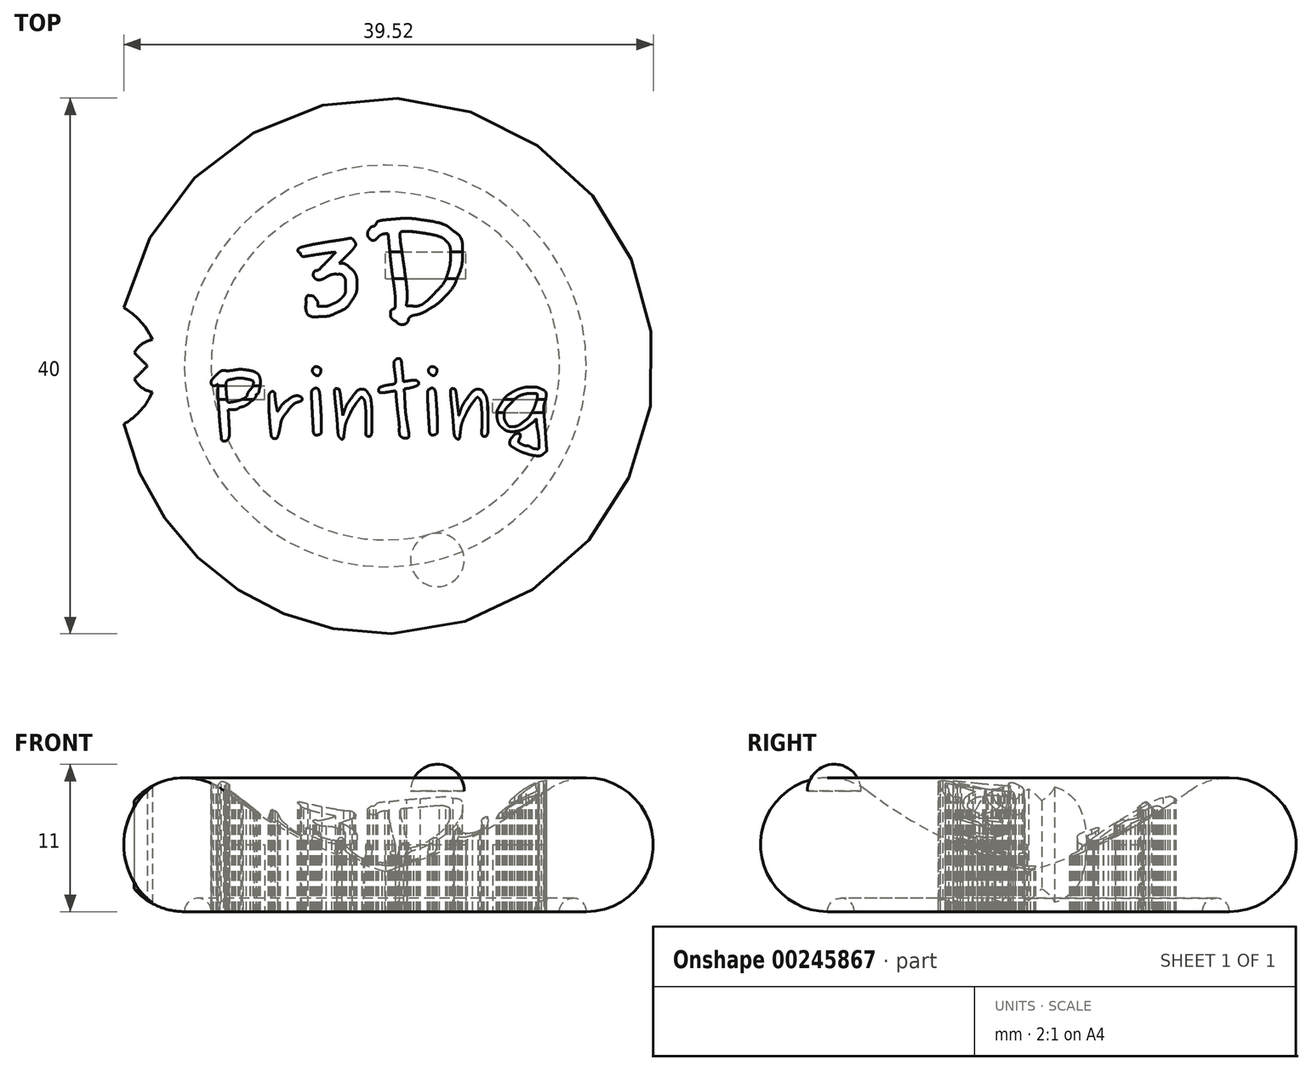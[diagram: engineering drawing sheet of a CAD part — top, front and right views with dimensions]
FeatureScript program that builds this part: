
annotation { "Feature Type Name" : "Feature", "Feature Type Description" : "" }
export const myFeature = defineFeature(function(context is Context, id is Id, definition is map)
    precondition{}
    {
        {
            var Q0;
            Q0=qCreatedBy(makeId("Front.planeOp"),FACE);
            var sketch = newSketch(context, id + "F0", { "sketchPlane" : qUnion([Q0])});
            skArc(sketch, "E0", {"start": v(-12, 9) * mm, "mid": v(-19.74, 6.58) * mm, "end": v(-15, 0) * mm});
            skLineSegment(sketch, "E1", {"start": v(-15, 0) * mm, "end": v(0, 0) * mm});
            skLineSegment(sketch, "E2", {"start": v(0, 0) * mm, "end": v(0, 3) * mm});
            skArc(sketch, "E3", {"start": v(-12, 9) * mm, "mid": v(-6.27, 5.46) * mm, "end": v(0, 3) * mm});
            skArc(sketch, "E4", {"start": v(-13, 0) * mm, "mid": v(-14, 1) * mm, "end": v(-15, 0) * mm});
            skSolve(sketch);
        }
        {
            var Q0;
            {var subQ3=sQuery(id+"F0.wireOp",EDGE,"E0");Q0=makeQuery(id+"F0.imprint","IMPRINT",FACE,{"disambiguationData":[TD([[makeQuery(id+"F0.imprint","IMPRINT",EDGE,{"derivedFrom":subQ3}),1.0]])]});}
            var Q1;
            Q1=sQuery(id+"F0.wireOp",EDGE,"E2");
            revolve(context, id + "F1", {"entities" : qUnion([Q0]), "axis" : qUnion([Q1]), "revolveType" : RevolveType.FULL});
        }
        {
            var Q0;
            Q0=qCreatedBy(makeId("Top.planeOp"),FACE);
            var sketch = newSketch(context, id + "F2", { "sketchPlane" : qUnion([Q0])});
            skCircle(sketch, "E5", {"center": v(-22, 0) * mm, "radius": 5 * mm});
            skCircle(sketch, "E6", {"center": v(-17, 0) * mm, "radius": 2 * mm});
            skLineSegment(sketch, "E7.bottom", {"start": v(-26.24, 0) * mm, "end": v(-22, 4.24) * mm});
            skLineSegment(sketch, "E7.top", {"start": v(-22, -4.24) * mm, "end": v(-17.76, 0) * mm});
            skLineSegment(sketch, "E7.left", {"start": v(-26.24, 0) * mm, "end": v(-22, -4.24) * mm});
            skLineSegment(sketch, "E7.right", {"start": v(-22, 4.24) * mm, "end": v(-17.76, 0) * mm});
            skLineSegment(sketch, "E8", {"start": v(-26.24, 0) * mm, "end": v(-17.76, 0) * mm, "construction": true});
            skSolve(sketch);
        }
        {
            var Q0;
            {var subQ0=sQuery(id+"F2.wireOp",EDGE,"E7.right");var subQ1=sQuery(id+"F2.wireOp",EDGE,"E6");var subQ2=makeQuery(id+"F2.imprint","INTERSECT",VERTEX,{"derivedFrom":[subQ1,subQ0]});Q0=makeQuery(id+"F2.imprint","IMPRINT",FACE,{"disambiguationData":[TD([[makeQuery(id+"F2.imprint","IMPRINT",EDGE,{"disambiguationData":[TD([[subQ2,-1.0]])],"derivedFrom":subQ1}),1.0]])]});}
            var Q1;
            {var subQ4=sQuery(id+"F2.wireOp",EDGE,"E7.bottom");Q1=makeQuery(id+"F2.imprint","IMPRINT",FACE,{"disambiguationData":[TD([[makeQuery(id+"F2.imprint","IMPRINT",EDGE,{"derivedFrom":subQ4}),-1.0]])]});}
            var Q2;
            {var subQ0=sQuery(id+"F2.wireOp",EDGE,"E7.bottom");Q2=makeQuery(id+"F2.imprint","IMPRINT",FACE,{"disambiguationData":[TD([[makeQuery(id+"F2.imprint","IMPRINT",EDGE,{"derivedFrom":subQ0}),1.0]])]});}
            extrude(context, id + "F3", {"entities" : qUnion([Q0, Q1, Q2]), "operationType" : NewBodyOperationType.REMOVE, "depth" : 25 * mm});
        }
        {
            var Q0;
            Q0=qCreatedBy(makeId("Right.planeOp"),FACE);
            var sketch = newSketch(context, id + "F4", { "sketchPlane" : qUnion([Q0])});
            skArc(sketch, "E9", {"start": v(-15, 11) * mm, "mid": v(-16.41, 10.41) * mm, "end": v(-17, 9) * mm});
            skLineSegment(sketch, "E10", {"start": v(-15, 11) * mm, "end": v(-15, 9) * mm});
            skLineSegment(sketch, "E11", {"start": v(-15, 9) * mm, "end": v(-17, 9) * mm});
            skSolve(sketch);
        }
        {
            var Q0;
            Q0=makeQuery(id+"F4.imprint","IMPRINT",FACE,{"disambiguationData":[TD([[makeQuery(id+"F4.imprint","IMPRINT",EDGE,{"derivedFrom":sQuery(id+"F4.wireOp",EDGE,"E9")}),1.0]])]});
            var Q1;
            Q1=sQuery(id+"F4.wireOp",EDGE,"E9");
            var Q2;
            Q2=sQuery(id+"F4.wireOp",EDGE,"E10");
            revolve(context, id + "F5", {"entities" : qUnion([Q0]), "surfaceEntities" : qUnion([Q1]), "axis" : qUnion([Q2]), "revolveType" : RevolveType.FULL});
        }
        {
            var Q0;
            Q0=qCreatedBy(makeId("Top.planeOp"),FACE);
            cPlane(context, id + "F6", {"entities" : qUnion([Q0]), "cplaneType" : CPlaneType.OFFSET, "offset" : 25 * mm, "width" : 150 * mm, "height" : 150 * mm});
        }
        {
            var Q0;
            Q0=qCreatedBy(id+"F6.planeOp",FACE);
            var sketch = newSketch(context, id + "F7", { "sketchPlane" : qUnion([Q0])});
            skFitSpline(sketch, "E12", {"points": [v(-4.86, 3.7) * mm, v(-5.56, 3.7) * mm, v(-5.9, 4.05) * mm, v(-5.9, 4.76) * mm]});
            skFitSpline(sketch, "E13", {"points": [v(-5.9, 4.76) * mm, v(-5.9, 5.08) * mm, v(-5.81, 5.24) * mm, v(-5.62, 5.24) * mm]});
            skFitSpline(sketch, "E14", {"points": [v(-5.62, 5.24) * mm, v(-5.46, 5.24) * mm, v(-5.33, 5.17) * mm, v(-5.21, 5.02) * mm]});
            skFitSpline(sketch, "E15", {"points": [v(-5.21, 5.02) * mm, v(-5.1, 4.86) * mm, v(-5.03, 4.7) * mm, v(-5.03, 4.55) * mm]});
            skFitSpline(sketch, "E16", {"points": [v(-5.03, 4.55) * mm, v(-5.03, 4.5) * mm, v(-5.02, 4.46) * mm, v(-5, 4.45) * mm]});
            skFitSpline(sketch, "E17", {"points": [v(-5, 4.45) * mm, v(-4.98, 4.44) * mm, v(-4.91, 4.44) * mm, v(-4.8, 4.44) * mm]});
            skFitSpline(sketch, "E18", {"points": [v(-4.8, 4.44) * mm, v(-4.51, 4.44) * mm, v(-4.24, 4.5) * mm, v(-3.98, 4.6) * mm]});
            skFitSpline(sketch, "E19", {"points": [v(-3.98, 4.6) * mm, v(-3.72, 4.72) * mm, v(-3.54, 4.82) * mm, v(-3.44, 4.9) * mm]});
            skFitSpline(sketch, "E20", {"points": [v(-3.44, 4.9) * mm, v(-3.34, 5) * mm, v(-3.26, 5.07) * mm, v(-3.2, 5.14) * mm]});
            skFitSpline(sketch, "E21", {"points": [v(-3.2, 5.14) * mm, v(-3.05, 5.31) * mm, v(-2.98, 5.6) * mm, v(-2.98, 5.98) * mm]});
            skFitSpline(sketch, "E22", {"points": [v(-2.98, 5.98) * mm, v(-2.98, 6.34) * mm, v(-3.02, 6.57) * mm, v(-3.12, 6.68) * mm]});
            skFitSpline(sketch, "E23", {"points": [v(-3.12, 6.68) * mm, v(-3.21, 6.79) * mm, v(-3.36, 6.84) * mm, v(-3.56, 6.84) * mm]});
            skFitSpline(sketch, "E24", {"points": [v(-3.56, 6.84) * mm, v(-3.87, 6.84) * mm, v(-4.15, 6.77) * mm, v(-4.4, 6.63) * mm]});
            skFitSpline(sketch, "E25", {"points": [v(-4.4, 6.63) * mm, v(-4.64, 6.5) * mm, v(-4.81, 6.43) * mm, v(-4.92, 6.43) * mm]});
            skFitSpline(sketch, "E26", {"points": [v(-4.92, 6.43) * mm, v(-5.07, 6.43) * mm, v(-5.18, 6.47) * mm, v(-5.26, 6.55) * mm]});
            skFitSpline(sketch, "E27", {"points": [v(-5.26, 6.55) * mm, v(-5.34, 6.63) * mm, v(-5.38, 6.72) * mm, v(-5.38, 6.83) * mm]});
            skFitSpline(sketch, "E28", {"points": [v(-5.38, 6.83) * mm, v(-5.38, 6.91) * mm, v(-5.36, 6.98) * mm, v(-5.31, 7.04) * mm]});
            skFitSpline(sketch, "E29", {"points": [v(-5.31, 7.04) * mm, v(-5.27, 7.1) * mm, v(-5.21, 7.12) * mm, v(-5.14, 7.12) * mm]});
            skFitSpline(sketch, "E30", {"points": [v(-5.14, 7.12) * mm, v(-5.04, 7.14) * mm, v(-4.8, 7.34) * mm, v(-4.43, 7.72) * mm]});
            skFitSpline(sketch, "E31", {"points": [v(-4.43, 7.72) * mm, v(-4.06, 8.1) * mm, v(-3.82, 8.36) * mm, v(-3.72, 8.5) * mm]});
            skFitSpline(sketch, "E32", {"points": [v(-3.72, 8.5) * mm, v(-3.94, 8.48) * mm, v(-4.25, 8.44) * mm, v(-4.63, 8.39) * mm]});
            skFitSpline(sketch, "E33", {"points": [v(-4.63, 8.39) * mm, v(-5, 8.33) * mm, v(-5.34, 8.28) * mm, v(-5.62, 8.23) * mm]});
            skFitSpline(sketch, "E34", {"points": [v(-5.62, 8.23) * mm, v(-5.91, 8.19) * mm, v(-6.07, 8.17) * mm, v(-6.1, 8.17) * mm]});
            skFitSpline(sketch, "E35", {"points": [v(-6.1, 8.17) * mm, v(-6.17, 8.17) * mm, v(-6.23, 8.19) * mm, v(-6.26, 8.22) * mm]});
            skFitSpline(sketch, "E36", {"points": [v(-6.26, 8.22) * mm, v(-6.3, 8.27) * mm, v(-6.32, 8.31) * mm, v(-6.33, 8.37) * mm]});
            skFitSpline(sketch, "E37", {"points": [v(-6.34, 8.44) * mm, v(-6.4, 8.45) * mm, v(-6.44, 8.47) * mm, v(-6.48, 8.5) * mm]});
            skFitSpline(sketch, "E38", {"points": [v(-6.48, 8.5) * mm, v(-6.52, 8.53) * mm, v(-6.54, 8.58) * mm, v(-6.54, 8.63) * mm]});
            skFitSpline(sketch, "E39", {"points": [v(-6.54, 8.63) * mm, v(-6.53, 8.7) * mm, v(-6.5, 8.75) * mm, v(-6.45, 8.78) * mm]});
            skFitSpline(sketch, "E40", {"points": [v(-6.45, 8.78) * mm, v(-6.36, 8.83) * mm, v(-6.15, 8.9) * mm, v(-5.8, 8.98) * mm]});
            skFitSpline(sketch, "E41", {"points": [v(-5.8, 8.98) * mm, v(-5.45, 9.06) * mm, v(-5.1, 9.13) * mm, v(-4.76, 9.18) * mm]});
            skFitSpline(sketch, "E42", {"points": [v(-4.76, 9.18) * mm, v(-4.4, 9.24) * mm, v(-4.05, 9.3) * mm, v(-3.69, 9.36) * mm]});
            skFitSpline(sketch, "E43", {"points": [v(-3.69, 9.36) * mm, v(-3.33, 9.41) * mm, v(-3.13, 9.44) * mm, v(-3.1, 9.45) * mm]});
            skFitSpline(sketch, "E44", {"points": [v(-3.1, 9.45) * mm, v(-2.8, 9.5) * mm, v(-2.65, 9.53) * mm, v(-2.64, 9.53) * mm]});
            skFitSpline(sketch, "E45", {"points": [v(-2.64, 9.53) * mm, v(-2.53, 9.53) * mm, v(-2.44, 9.47) * mm, v(-2.35, 9.36) * mm]});
            skFitSpline(sketch, "E46", {"points": [v(-2.35, 9.36) * mm, v(-2.26, 9.25) * mm, v(-2.22, 9.15) * mm, v(-2.22, 9.06) * mm]});
            skFitSpline(sketch, "E47", {"points": [v(-2.22, 9.06) * mm, v(-2.22, 9.02) * mm, v(-2.24, 8.96) * mm, v(-2.3, 8.88) * mm]});
            skFitSpline(sketch, "E48", {"points": [v(-2.3, 8.88) * mm, v(-2.34, 8.8) * mm, v(-2.41, 8.72) * mm, v(-2.5, 8.6) * mm]});
            skFitSpline(sketch, "E49", {"points": [v(-2.5, 8.6) * mm, v(-2.6, 8.5) * mm, v(-2.7, 8.4) * mm, v(-2.8, 8.31) * mm]});
            skFitSpline(sketch, "E50", {"points": [v(-2.8, 8.31) * mm, v(-2.88, 8.23) * mm, v(-3, 8.12) * mm, v(-3.13, 7.98) * mm]});
            skFitSpline(sketch, "E51", {"points": [v(-3.13, 7.98) * mm, v(-3.27, 7.84) * mm, v(-3.38, 7.73) * mm, v(-3.45, 7.65) * mm]});
            skLineSegment(sketch, "E52", {"start": v(-6.33, 8.37) * mm, "end": v(-6.34, 8.44) * mm});
            skLineSegment(sketch, "E53", {"start": v(-6.34, 8.44) * mm, "end": v(-6.33, 8.37) * mm});
            skFitSpline(sketch, "E54", {"points": [v(-3.32, 7.65) * mm, v(-3.1, 7.65) * mm, v(-2.88, 7.53) * mm, v(-2.63, 7.3) * mm]});
            skFitSpline(sketch, "E55", {"points": [v(-2.63, 7.3) * mm, v(-2.38, 7.1) * mm, v(-2.22, 6.86) * mm, v(-2.15, 6.62) * mm]});
            skFitSpline(sketch, "E56", {"points": [v(-2.15, 6.62) * mm, v(-2.13, 6.53) * mm, v(-2.12, 6.4) * mm, v(-2.12, 6.26) * mm]});
            skFitSpline(sketch, "E57", {"points": [v(-2.12, 6.26) * mm, v(-2.12, 5.74) * mm, v(-2.25, 5.26) * mm, v(-2.53, 4.84) * mm]});
            skFitSpline(sketch, "E58", {"points": [v(-2.53, 4.84) * mm, v(-2.75, 4.5) * mm, v(-3.09, 4.22) * mm, v(-3.54, 4.01) * mm]});
            skFitSpline(sketch, "E59", {"points": [v(-3.54, 4.01) * mm, v(-4, 3.8) * mm, v(-4.44, 3.7) * mm, v(-4.86, 3.7) * mm]});
            skLineSegment(sketch, "E60", {"start": v(-3.45, 7.65) * mm, "end": v(-3.32, 7.65) * mm});
            skLineSegment(sketch, "E61", {"start": v(-3.32, 7.65) * mm, "end": v(-3.45, 7.65) * mm});
            skFitSpline(sketch, "E62", {"points": [v(1.44, 10.04) * mm, v(1.3, 10.04) * mm, v(1.2, 10.03) * mm, v(1.16, 10) * mm]});
            skFitSpline(sketch, "E63", {"points": [v(1.16, 10) * mm, v(1.12, 9.96) * mm, v(1.1, 9.89) * mm, v(1.1, 9.76) * mm]});
            skFitSpline(sketch, "E64", {"points": [v(1.1, 9.76) * mm, v(1.1, 9.56) * mm, v(1.2, 8.85) * mm, v(1.36, 7.61) * mm]});
            skFitSpline(sketch, "E65", {"points": [v(1.36, 7.61) * mm, v(1.54, 6.38) * mm, v(1.63, 5.57) * mm, v(1.63, 5.2) * mm]});
            skFitSpline(sketch, "E66", {"points": [v(1.63, 5.2) * mm, v(1.63, 5.06) * mm, v(1.62, 4.93) * mm, v(1.6, 4.8) * mm]});
            skFitSpline(sketch, "E67", {"points": [v(1.93, 4.48) * mm, v(2.47, 4.48) * mm, v(3.1, 4.85) * mm, v(3.82, 5.6) * mm]});
            skFitSpline(sketch, "E68", {"points": [v(3.82, 5.6) * mm, v(4.23, 6.01) * mm, v(4.5, 6.44) * mm, v(4.64, 6.87) * mm]});
            skFitSpline(sketch, "E69", {"points": [v(4.64, 6.87) * mm, v(4.78, 7.3) * mm, v(4.85, 7.83) * mm, v(4.85, 8.46) * mm]});
            skFitSpline(sketch, "E70", {"points": [v(4.85, 8.46) * mm, v(4.85, 8.71) * mm, v(4.83, 8.88) * mm, v(4.8, 8.97) * mm]});
            skFitSpline(sketch, "E71", {"points": [v(4.8, 8.97) * mm, v(4.76, 9.06) * mm, v(4.67, 9.18) * mm, v(4.53, 9.33) * mm]});
            skFitSpline(sketch, "E72", {"points": [v(4.53, 9.33) * mm, v(4.39, 9.47) * mm, v(4.22, 9.58) * mm, v(4.05, 9.65) * mm]});
            skFitSpline(sketch, "E73", {"points": [v(4.05, 9.65) * mm, v(3.88, 9.71) * mm, v(3.59, 9.78) * mm, v(3.18, 9.86) * mm]});
            skFitSpline(sketch, "E74", {"points": [v(3.18, 9.86) * mm, v(2.4, 9.98) * mm, v(1.83, 10.04) * mm, v(1.44, 10.04) * mm]});
            skLineSegment(sketch, "E75", {"start": v(1.6, 4.8) * mm, "end": v(1.55, 4.48) * mm});
            skLineSegment(sketch, "E76", {"start": v(1.55, 4.48) * mm, "end": v(1.93, 4.48) * mm});
            skFitSpline(sketch, "E77", {"points": [v(-1.33, 9.83) * mm, v(-1.32, 9.98) * mm, v(-1.27, 10.11) * mm, v(-1.17, 10.23) * mm]});
            skFitSpline(sketch, "E78", {"points": [v(-1.17, 10.23) * mm, v(-1.07, 10.36) * mm, v(-0.97, 10.42) * mm, v(-0.88, 10.42) * mm]});
            skFitSpline(sketch, "E79", {"points": [v(-0.88, 10.42) * mm, v(-0.82, 10.44) * mm, v(-0.76, 10.5) * mm, v(-0.7, 10.58) * mm]});
            skFitSpline(sketch, "E80", {"points": [v(-0.7, 10.58) * mm, v(-0.59, 10.76) * mm, v(-0.26, 10.87) * mm, v(0.28, 10.93) * mm]});
            skFitSpline(sketch, "E81", {"points": [v(0.28, 10.93) * mm, v(0.92, 10.99) * mm, v(1.36, 11.02) * mm, v(1.6, 11.02) * mm]});
            skFitSpline(sketch, "E82", {"points": [v(1.6, 11.02) * mm, v(1.88, 11.02) * mm, v(2.22, 10.98) * mm, v(2.62, 10.92) * mm]});
            skFitSpline(sketch, "E83", {"points": [v(2.62, 10.92) * mm, v(3.77, 10.74) * mm, v(4.58, 10.46) * mm, v(5.04, 10.1) * mm]});
            skFitSpline(sketch, "E84", {"points": [v(5.04, 10.1) * mm, v(5.51, 9.74) * mm, v(5.75, 9.2) * mm, v(5.75, 8.46) * mm]});
            skFitSpline(sketch, "E85", {"points": [v(5.75, 8.46) * mm, v(5.75, 7.83) * mm, v(5.63, 7.23) * mm, v(5.4, 6.66) * mm]});
            skFitSpline(sketch, "E86", {"points": [v(5.4, 6.66) * mm, v(5.17, 6.1) * mm, v(4.87, 5.62) * mm, v(4.5, 5.24) * mm]});
            skFitSpline(sketch, "E87", {"points": [v(4.5, 5.24) * mm, v(4.14, 4.85) * mm, v(3.75, 4.54) * mm, v(3.33, 4.29) * mm]});
            skFitSpline(sketch, "E88", {"points": [v(3.33, 4.29) * mm, v(2.93, 4.04) * mm, v(2.52, 3.87) * mm, v(2.13, 3.78) * mm]});
            skFitSpline(sketch, "E89", {"points": [v(2.13, 3.78) * mm, v(2, 3.75) * mm, v(1.9, 3.7) * mm, v(1.83, 3.64) * mm]});
            skFitSpline(sketch, "E90", {"points": [v(1.83, 3.64) * mm, v(1.76, 3.57) * mm, v(1.72, 3.5) * mm, v(1.72, 3.45) * mm]});
            skFitSpline(sketch, "E91", {"points": [v(1.72, 3.45) * mm, v(1.71, 3.38) * mm, v(1.69, 3.32) * mm, v(1.64, 3.26) * mm]});
            skFitSpline(sketch, "E92", {"points": [v(1.64, 3.26) * mm, v(1.6, 3.2) * mm, v(1.54, 3.15) * mm, v(1.44, 3.12) * mm]});
            skFitSpline(sketch, "E93", {"points": [v(1.44, 3.12) * mm, v(1.38, 3.1) * mm, v(1.32, 3.09) * mm, v(1.25, 3.09) * mm]});
            skFitSpline(sketch, "E94", {"points": [v(1.25, 3.09) * mm, v(1.14, 3.09) * mm, v(1.05, 3.11) * mm, v(0.97, 3.15) * mm]});
            skFitSpline(sketch, "E95", {"points": [v(0.97, 3.15) * mm, v(0.9, 3.19) * mm, v(0.86, 3.24) * mm, v(0.85, 3.3) * mm]});
            skFitSpline(sketch, "E96", {"points": [v(0.71, 3.36) * mm, v(0.62, 3.4) * mm, v(0.54, 3.47) * mm, v(0.48, 3.55) * mm]});
            skFitSpline(sketch, "E97", {"points": [v(0.48, 3.55) * mm, v(0.41, 3.62) * mm, v(0.38, 3.72) * mm, v(0.38, 3.85) * mm]});
            skFitSpline(sketch, "E98", {"points": [v(0.38, 3.85) * mm, v(0.38, 4.06) * mm, v(0.47, 4.2) * mm, v(0.63, 4.26) * mm]});
            skFitSpline(sketch, "E99", {"points": [v(0.63, 4.26) * mm, v(0.7, 4.3) * mm, v(0.73, 4.52) * mm, v(0.73, 4.9) * mm]});
            skFitSpline(sketch, "E100", {"points": [v(0.73, 4.9) * mm, v(0.73, 5.14) * mm, v(0.72, 5.39) * mm, v(0.69, 5.64) * mm]});
            skFitSpline(sketch, "E101", {"points": [v(0.69, 5.64) * mm, v(0.66, 5.89) * mm, v(0.6, 6.26) * mm, v(0.53, 6.77) * mm]});
            skFitSpline(sketch, "E102", {"points": [v(0.53, 6.77) * mm, v(0.46, 7.28) * mm, v(0.4, 7.85) * mm, v(0.34, 8.47) * mm]});
            skLineSegment(sketch, "E103", {"start": v(0.85, 3.3) * mm, "end": v(0.71, 3.36) * mm});
            skLineSegment(sketch, "E104", {"start": v(0.71, 3.36) * mm, "end": v(0.85, 3.3) * mm});
            skFitSpline(sketch, "E105", {"points": [v(0, 9.87) * mm, v(-0.2, 9.84) * mm, v(-0.38, 9.75) * mm, v(-0.55, 9.6) * mm]});
            skFitSpline(sketch, "E106", {"points": [v(-0.55, 9.6) * mm, v(-0.72, 9.44) * mm, v(-0.84, 9.36) * mm, v(-0.91, 9.36) * mm]});
            skFitSpline(sketch, "E107", {"points": [v(-0.91, 9.36) * mm, v(-1, 9.36) * mm, v(-1.08, 9.42) * mm, v(-1.19, 9.52) * mm]});
            skFitSpline(sketch, "E108", {"points": [v(-1.19, 9.52) * mm, v(-1.28, 9.63) * mm, v(-1.33, 9.73) * mm, v(-1.33, 9.83) * mm]});
            skLineSegment(sketch, "E109", {"start": v(0.34, 8.47) * mm, "end": v(0.2, 9.89) * mm});
            skLineSegment(sketch, "E110", {"start": v(0.2, 9.89) * mm, "end": v(0, 9.87) * mm});
            skFitSpline(sketch, "E111", {"points": [v(-9.86, -1.36) * mm, v(-9.86, -1.18) * mm, v(-10.03, -1.05) * mm, v(-10.39, -0.98) * mm]});
            skFitSpline(sketch, "E112", {"points": [v(-10.39, -0.98) * mm, v(-10.62, -0.93) * mm, v(-10.77, -0.9) * mm, v(-10.85, -0.9) * mm]});
            skFitSpline(sketch, "E113", {"points": [v(-10.85, -0.9) * mm, v(-10.92, -0.9) * mm, v(-11.12, -0.93) * mm, v(-11.43, -1) * mm]});
            skFitSpline(sketch, "E114", {"points": [v(-11.43, -1) * mm, v(-11.65, -1.04) * mm, v(-11.77, -1.08) * mm, v(-11.82, -1.13) * mm]});
            skFitSpline(sketch, "E115", {"points": [v(-11.82, -1.13) * mm, v(-11.86, -1.18) * mm, v(-11.88, -1.3) * mm, v(-11.88, -1.53) * mm]});
            skFitSpline(sketch, "E116", {"points": [v(-11.88, -1.53) * mm, v(-11.88, -1.74) * mm, v(-11.87, -1.98) * mm, v(-11.85, -2.24) * mm]});
            skFitSpline(sketch, "E117", {"points": [v(-11.85, -2.24) * mm, v(-11.82, -2.5) * mm, v(-11.8, -2.65) * mm, v(-11.76, -2.7) * mm]});
            skFitSpline(sketch, "E118", {"points": [v(-11.76, -2.7) * mm, v(-11.75, -2.71) * mm, v(-11.73, -2.71) * mm, v(-11.69, -2.71) * mm]});
            skFitSpline(sketch, "E119", {"points": [v(-11.69, -2.71) * mm, v(-11.56, -2.71) * mm, v(-11.39, -2.69) * mm, v(-11.15, -2.63) * mm]});
            skFitSpline(sketch, "E120", {"points": [v(-11.15, -2.63) * mm, v(-10.92, -2.58) * mm, v(-10.73, -2.52) * mm, v(-10.58, -2.44) * mm]});
            skFitSpline(sketch, "E121", {"points": [v(-10.58, -2.44) * mm, v(-10.5, -2.4) * mm, v(-10.44, -2.35) * mm, v(-10.39, -2.3) * mm]});
            skFitSpline(sketch, "E122", {"points": [v(-10.39, -2.3) * mm, v(-10.33, -2.24) * mm, v(-10.3, -2.2) * mm, v(-10.3, -2.16) * mm]});
            skFitSpline(sketch, "E123", {"points": [v(-10.3, -2.16) * mm, v(-10.29, -2.06) * mm, v(-10.21, -1.93) * mm, v(-10.07, -1.76) * mm]});
            skFitSpline(sketch, "E124", {"points": [v(-10.07, -1.76) * mm, v(-9.93, -1.58) * mm, v(-9.86, -1.45) * mm, v(-9.86, -1.36) * mm]});
            skFitSpline(sketch, "E125", {"points": [v(-11.8, -0.36) * mm, v(-11.67, -0.36) * mm, v(-11.5, -0.35) * mm, v(-11.3, -0.31) * mm]});
            skFitSpline(sketch, "E126", {"points": [v(-11.3, -0.31) * mm, v(-11.1, -0.28) * mm, v(-10.92, -0.26) * mm, v(-10.78, -0.26) * mm]});
            skFitSpline(sketch, "E127", {"points": [v(-10.78, -0.26) * mm, v(-10.73, -0.26) * mm, v(-10.68, -0.26) * mm, v(-10.65, -0.26) * mm]});
            skFitSpline(sketch, "E128", {"points": [v(-10.65, -0.26) * mm, v(-10.5, -0.28) * mm, v(-10.38, -0.3) * mm, v(-10.32, -0.3) * mm]});
            skFitSpline(sketch, "E129", {"points": [v(-10.32, -0.3) * mm, v(-10.25, -0.32) * mm, v(-10.16, -0.33) * mm, v(-10.05, -0.36) * mm]});
            skFitSpline(sketch, "E130", {"points": [v(-10.05, -0.36) * mm, v(-9.92, -0.38) * mm, v(-9.84, -0.4) * mm, v(-9.79, -0.43) * mm]});
            skFitSpline(sketch, "E131", {"points": [v(-9.79, -0.43) * mm, v(-9.74, -0.45) * mm, v(-9.67, -0.49) * mm, v(-9.6, -0.53) * mm]});
            skFitSpline(sketch, "E132", {"points": [v(-9.6, -0.53) * mm, v(-9.53, -0.58) * mm, v(-9.48, -0.63) * mm, v(-9.45, -0.7) * mm]});
            skFitSpline(sketch, "E133", {"points": [v(-9.45, -0.7) * mm, v(-9.42, -0.75) * mm, v(-9.39, -0.82) * mm, v(-9.36, -0.9) * mm]});
            skFitSpline(sketch, "E134", {"points": [v(-9.36, -0.9) * mm, v(-9.34, -0.99) * mm, v(-9.33, -1.09) * mm, v(-9.33, -1.2) * mm]});
            skFitSpline(sketch, "E135", {"points": [v(-9.33, -1.2) * mm, v(-9.33, -1.37) * mm, v(-9.35, -1.57) * mm, v(-9.4, -1.78) * mm]});
            skFitSpline(sketch, "E136", {"points": [v(-9.4, -1.78) * mm, v(-9.45, -2) * mm, v(-9.53, -2.1) * mm, v(-9.62, -2.1) * mm]});
            skFitSpline(sketch, "E137", {"points": [v(-9.62, -2.1) * mm, v(-9.62, -2.11) * mm, v(-9.63, -2.13) * mm, v(-9.63, -2.15) * mm]});
            skFitSpline(sketch, "E138", {"points": [v(-9.63, -2.15) * mm, v(-9.63, -2.18) * mm, v(-9.63, -2.2) * mm, v(-9.63, -2.2) * mm]});
            skFitSpline(sketch, "E139", {"points": [v(-9.63, -2.2) * mm, v(-9.68, -2.32) * mm, v(-9.82, -2.49) * mm, v(-10.08, -2.7) * mm]});
            skFitSpline(sketch, "E140", {"points": [v(-10.08, -2.7) * mm, v(-10.33, -2.9) * mm, v(-10.53, -3.02) * mm, v(-10.69, -3.05) * mm]});
            skFitSpline(sketch, "E141", {"points": [v(-10.69, -3.05) * mm, v(-10.77, -3.07) * mm, v(-10.84, -3.1) * mm, v(-10.87, -3.1) * mm]});
            skFitSpline(sketch, "E142", {"points": [v(-10.87, -3.1) * mm, v(-10.9, -3.11) * mm, v(-10.93, -3.13) * mm, v(-10.95, -3.15) * mm]});
            skFitSpline(sketch, "E143", {"points": [v(-10.95, -3.15) * mm, v(-10.96, -3.17) * mm, v(-10.97, -3.18) * mm, v(-10.98, -3.18) * mm]});
            skFitSpline(sketch, "E144", {"points": [v(-10.98, -3.18) * mm, v(-11.06, -3.23) * mm, v(-11.21, -3.25) * mm, v(-11.44, -3.25) * mm]});
            skFitSpline(sketch, "E145", {"points": [v(-11.68, -4.24) * mm, v(-11.66, -4.58) * mm, v(-11.65, -4.82) * mm, v(-11.65, -4.97) * mm]});
            skFitSpline(sketch, "E146", {"points": [v(-11.65, -4.97) * mm, v(-11.65, -5.16) * mm, v(-11.67, -5.3) * mm, v(-11.7, -5.4) * mm]});
            skFitSpline(sketch, "E147", {"points": [v(-11.7, -5.4) * mm, v(-11.74, -5.49) * mm, v(-11.8, -5.55) * mm, v(-11.9, -5.6) * mm]});
            skFitSpline(sketch, "E148", {"points": [v(-11.9, -5.6) * mm, v(-11.94, -5.61) * mm, v(-11.97, -5.62) * mm, v(-12, -5.62) * mm]});
            skFitSpline(sketch, "E149", {"points": [v(-12, -5.62) * mm, v(-12.14, -5.62) * mm, v(-12.22, -5.5) * mm, v(-12.25, -5.28) * mm]});
            skFitSpline(sketch, "E150", {"points": [v(-12.25, -5.28) * mm, v(-12.3, -4.97) * mm, v(-12.35, -4.4) * mm, v(-12.4, -3.55) * mm]});
            skFitSpline(sketch, "E151", {"points": [v(-12.4, -3.55) * mm, v(-12.47, -2.7) * mm, v(-12.5, -2.13) * mm, v(-12.5, -1.84) * mm]});
            skLineSegment(sketch, "E152", {"start": v(-11.44, -3.25) * mm, "end": v(-11.73, -3.25) * mm});
            skLineSegment(sketch, "E153", {"start": v(-11.73, -3.25) * mm, "end": v(-11.68, -4.24) * mm});
            skFitSpline(sketch, "E154", {"points": [v(-12.55, -1.4) * mm, v(-12.64, -1.46) * mm, v(-12.73, -1.49) * mm, v(-12.81, -1.49) * mm]});
            skFitSpline(sketch, "E155", {"points": [v(-12.81, -1.49) * mm, v(-12.86, -1.49) * mm, v(-12.9, -1.47) * mm, v(-12.94, -1.43) * mm]});
            skFitSpline(sketch, "E156", {"points": [v(-12.94, -1.43) * mm, v(-12.99, -1.39) * mm, v(-13, -1.33) * mm, v(-13, -1.27) * mm]});
            skFitSpline(sketch, "E157", {"points": [v(-13, -1.27) * mm, v(-13, -1.14) * mm, v(-12.88, -0.95) * mm, v(-12.63, -0.7) * mm]});
            skFitSpline(sketch, "E158", {"points": [v(-12.63, -0.7) * mm, v(-12.5, -0.56) * mm, v(-12.4, -0.47) * mm, v(-12.33, -0.42) * mm]});
            skFitSpline(sketch, "E159", {"points": [v(-12.33, -0.42) * mm, v(-12.25, -0.37) * mm, v(-12.17, -0.34) * mm, v(-12.09, -0.34) * mm]});
            skFitSpline(sketch, "E160", {"points": [v(-12.09, -0.34) * mm, v(-12.05, -0.34) * mm, v(-12.01, -0.35) * mm, v(-11.96, -0.36) * mm]});
            skFitSpline(sketch, "E161", {"points": [v(-11.96, -0.36) * mm, v(-11.92, -0.36) * mm, v(-11.86, -0.36) * mm, v(-11.8, -0.36) * mm]});
            skLineSegment(sketch, "E162", {"start": v(-12.5, -1.84) * mm, "end": v(-12.5, -1.35) * mm});
            skLineSegment(sketch, "E163", {"start": v(-12.5, -1.35) * mm, "end": v(-12.55, -1.4) * mm});
            skFitSpline(sketch, "E164", {"points": [v(-6.56, -2.23) * mm, v(-6.48, -2.23) * mm, v(-6.41, -2.25) * mm, v(-6.35, -2.29) * mm]});
            skFitSpline(sketch, "E165", {"points": [v(-6.35, -2.29) * mm, v(-6.3, -2.32) * mm, v(-6.26, -2.35) * mm, v(-6.24, -2.38) * mm]});
            skFitSpline(sketch, "E166", {"points": [v(-6.24, -2.38) * mm, v(-6.22, -2.42) * mm, v(-6.21, -2.44) * mm, v(-6.21, -2.47) * mm]});
            skFitSpline(sketch, "E167", {"points": [v(-6.21, -2.47) * mm, v(-6.21, -2.55) * mm, v(-6.3, -2.63) * mm, v(-6.5, -2.7) * mm]});
            skFitSpline(sketch, "E168", {"points": [v(-6.5, -2.7) * mm, v(-6.74, -2.79) * mm, v(-7.01, -3.02) * mm, v(-7.3, -3.38) * mm]});
            skFitSpline(sketch, "E169", {"points": [v(-7.3, -3.38) * mm, v(-7.6, -3.75) * mm, v(-7.77, -4.1) * mm, v(-7.83, -4.41) * mm]});
            skFitSpline(sketch, "E170", {"points": [v(-7.83, -4.41) * mm, v(-7.9, -4.82) * mm, v(-7.97, -5.1) * mm, v(-8.02, -5.23) * mm]});
            skFitSpline(sketch, "E171", {"points": [v(-8.02, -5.23) * mm, v(-8.08, -5.37) * mm, v(-8.15, -5.43) * mm, v(-8.25, -5.43) * mm]});
            skFitSpline(sketch, "E172", {"points": [v(-8.25, -5.43) * mm, v(-8.3, -5.43) * mm, v(-8.33, -5.43) * mm, v(-8.36, -5.42) * mm]});
            skFitSpline(sketch, "E173", {"points": [v(-8.36, -5.42) * mm, v(-8.4, -5.4) * mm, v(-8.42, -5.4) * mm, v(-8.44, -5.36) * mm]});
            skFitSpline(sketch, "E174", {"points": [v(-8.44, -5.36) * mm, v(-8.46, -5.33) * mm, v(-8.47, -5.3) * mm, v(-8.49, -5.29) * mm]});
            skFitSpline(sketch, "E175", {"points": [v(-8.49, -5.29) * mm, v(-8.5, -5.27) * mm, v(-8.51, -5.24) * mm, v(-8.52, -5.2) * mm]});
            skFitSpline(sketch, "E176", {"points": [v(-8.52, -5.2) * mm, v(-8.53, -5.14) * mm, v(-8.54, -5.1) * mm, v(-8.54, -5.09) * mm]});
            skFitSpline(sketch, "E177", {"points": [v(-8.54, -5.09) * mm, v(-8.54, -5.06) * mm, v(-8.54, -5.02) * mm, v(-8.55, -4.97) * mm]});
            skFitSpline(sketch, "E178", {"points": [v(-8.55, -4.97) * mm, v(-8.56, -4.92) * mm, v(-8.56, -4.88) * mm, v(-8.56, -4.87) * mm]});
            skFitSpline(sketch, "E179", {"points": [v(-8.56, -4.87) * mm, v(-8.66, -3.92) * mm, v(-8.7, -3.12) * mm, v(-8.7, -2.48) * mm]});
            skFitSpline(sketch, "E180", {"points": [v(-8.7, -2.48) * mm, v(-8.7, -2.34) * mm, v(-8.7, -2.24) * mm, v(-8.68, -2.16) * mm]});
            skFitSpline(sketch, "E181", {"points": [v(-8.68, -2.16) * mm, v(-8.66, -2.09) * mm, v(-8.62, -2.02) * mm, v(-8.56, -1.96) * mm]});
            skFitSpline(sketch, "E182", {"points": [v(-8.56, -1.96) * mm, v(-8.52, -1.93) * mm, v(-8.47, -1.9) * mm, v(-8.42, -1.9) * mm]});
            skFitSpline(sketch, "E183", {"points": [v(-8.42, -1.9) * mm, v(-8.37, -1.9) * mm, v(-8.33, -1.93) * mm, v(-8.3, -1.98) * mm]});
            skFitSpline(sketch, "E184", {"points": [v(-8.3, -1.98) * mm, v(-8.25, -2.02) * mm, v(-8.24, -2.07) * mm, v(-8.24, -2.14) * mm]});
            skFitSpline(sketch, "E185", {"points": [v(-8.24, -2.14) * mm, v(-8.24, -2.3) * mm, v(-8.22, -2.5) * mm, v(-8.18, -2.78) * mm]});
            skFitSpline(sketch, "E186", {"points": [v(-8.18, -2.78) * mm, v(-8.13, -3.05) * mm, v(-8.1, -3.26) * mm, v(-8.05, -3.42) * mm]});
            skFitSpline(sketch, "E187", {"points": [v(-8.05, -3.42) * mm, v(-8.02, -3.37) * mm, v(-7.97, -3.3) * mm, v(-7.91, -3.21) * mm]});
            skFitSpline(sketch, "E188", {"points": [v(-7.91, -3.21) * mm, v(-7.76, -2.96) * mm, v(-7.54, -2.74) * mm, v(-7.27, -2.54) * mm]});
            skFitSpline(sketch, "E189", {"points": [v(-7.27, -2.54) * mm, v(-7, -2.33) * mm, v(-6.75, -2.23) * mm, v(-6.56, -2.23) * mm]});
            skFitSpline(sketch, "E190", {"points": [v(-5.37, -1.73) * mm, v(-5.3, -1.68) * mm, v(-5.24, -1.66) * mm, v(-5.17, -1.66) * mm]});
            skFitSpline(sketch, "E191", {"points": [v(-5.17, -1.66) * mm, v(-5.1, -1.66) * mm, v(-5.05, -1.69) * mm, v(-5, -1.74) * mm]});
            skFitSpline(sketch, "E192", {"points": [v(-5, -1.74) * mm, v(-4.94, -1.86) * mm, v(-4.89, -2.21) * mm, v(-4.85, -2.8) * mm]});
            skFitSpline(sketch, "E193", {"points": [v(-4.85, -2.8) * mm, v(-4.8, -3.38) * mm, v(-4.78, -3.93) * mm, v(-4.78, -4.44) * mm]});
            skFitSpline(sketch, "E194", {"points": [v(-4.78, -4.44) * mm, v(-4.78, -4.8) * mm, v(-4.8, -5) * mm, v(-4.82, -5.06) * mm]});
            skFitSpline(sketch, "E195", {"points": [v(-4.82, -5.06) * mm, v(-4.9, -5.12) * mm, v(-4.99, -5.15) * mm, v(-5.08, -5.15) * mm]});
            skFitSpline(sketch, "E196", {"points": [v(-5.08, -5.15) * mm, v(-5.22, -5.15) * mm, v(-5.31, -5.11) * mm, v(-5.34, -5.03) * mm]});
            skFitSpline(sketch, "E197", {"points": [v(-5.34, -5.03) * mm, v(-5.36, -4.96) * mm, v(-5.4, -4.54) * mm, v(-5.44, -3.76) * mm]});
            skFitSpline(sketch, "E198", {"points": [v(-5.44, -3.76) * mm, v(-5.48, -2.98) * mm, v(-5.5, -2.45) * mm, v(-5.5, -2.19) * mm]});
            skFitSpline(sketch, "E199", {"points": [v(-5.5, -2.19) * mm, v(-5.5, -1.94) * mm, v(-5.46, -1.79) * mm, v(-5.37, -1.73) * mm]});
            skFitSpline(sketch, "E200", {"points": [v(-5.44, -0.3) * mm, v(-5.43, -0.23) * mm, v(-5.4, -0.17) * mm, v(-5.34, -0.12) * mm]});
            skFitSpline(sketch, "E201", {"points": [v(-5.34, -0.12) * mm, v(-5.28, -0.07) * mm, v(-5.22, -0.05) * mm, v(-5.17, -0.05) * mm]});
            skFitSpline(sketch, "E202", {"points": [v(-5.17, -0.05) * mm, v(-5.1, -0.05) * mm, v(-5.04, -0.07) * mm, v(-4.95, -0.12) * mm]});
            skFitSpline(sketch, "E203", {"points": [v(-4.95, -0.12) * mm, v(-4.86, -0.18) * mm, v(-4.81, -0.25) * mm, v(-4.81, -0.34) * mm]});
            skFitSpline(sketch, "E204", {"points": [v(-4.81, -0.34) * mm, v(-4.81, -0.44) * mm, v(-4.84, -0.52) * mm, v(-4.89, -0.6) * mm]});
            skFitSpline(sketch, "E205", {"points": [v(-4.89, -0.6) * mm, v(-4.93, -0.68) * mm, v(-5, -0.72) * mm, v(-5.08, -0.72) * mm]});
            skFitSpline(sketch, "E206", {"points": [v(-5.08, -0.72) * mm, v(-5.17, -0.72) * mm, v(-5.25, -0.68) * mm, v(-5.32, -0.6) * mm]});
            skFitSpline(sketch, "E207", {"points": [v(-5.32, -0.6) * mm, v(-5.4, -0.52) * mm, v(-5.44, -0.42) * mm, v(-5.44, -0.3) * mm]});
            skFitSpline(sketch, "E208", {"points": [v(-3.8, -2.02) * mm, v(-3.8, -1.8) * mm, v(-3.72, -1.7) * mm, v(-3.6, -1.7) * mm]});
            skFitSpline(sketch, "E209", {"points": [v(-3.6, -1.7) * mm, v(-3.5, -1.7) * mm, v(-3.44, -1.76) * mm, v(-3.41, -1.87) * mm]});
            skFitSpline(sketch, "E210", {"points": [v(-3.41, -1.87) * mm, v(-3.39, -1.97) * mm, v(-3.34, -2.27) * mm, v(-3.3, -2.76) * mm]});
            skFitSpline(sketch, "E211", {"points": [v(-3.3, -2.76) * mm, v(-3.28, -2.86) * mm, v(-3.27, -2.95) * mm, v(-3.26, -3.01) * mm]});
            skFitSpline(sketch, "E212", {"points": [v(-3.1, -3.5) * mm, v(-3.02, -3.24) * mm, v(-2.95, -3.05) * mm, v(-2.9, -2.93) * mm]});
            skFitSpline(sketch, "E213", {"points": [v(-2.9, -2.93) * mm, v(-2.83, -2.8) * mm, v(-2.7, -2.63) * mm, v(-2.54, -2.4) * mm]});
            skFitSpline(sketch, "E214", {"points": [v(-2.54, -2.4) * mm, v(-2.2, -1.97) * mm, v(-1.93, -1.76) * mm, v(-1.7, -1.76) * mm]});
            skFitSpline(sketch, "E215", {"points": [v(-1.7, -1.76) * mm, v(-1.55, -1.76) * mm, v(-1.42, -1.84) * mm, v(-1.31, -2) * mm]});
            skFitSpline(sketch, "E216", {"points": [v(-1.31, -2) * mm, v(-1.18, -2.19) * mm, v(-1.1, -2.37) * mm, v(-1.08, -2.55) * mm]});
            skFitSpline(sketch, "E217", {"points": [v(-1.08, -2.55) * mm, v(-1.04, -2.74) * mm, v(-1.02, -3.16) * mm, v(-1, -3.8) * mm]});
            skFitSpline(sketch, "E218", {"points": [v(-1, -3.8) * mm, v(-1, -4.22) * mm, v(-1, -4.47) * mm, v(-1, -4.56) * mm]});
            skFitSpline(sketch, "E219", {"points": [v(-1, -4.56) * mm, v(-1, -4.83) * mm, v(-1.01, -5.01) * mm, v(-1.05, -5.11) * mm]});
            skFitSpline(sketch, "E220", {"points": [v(-1.05, -5.11) * mm, v(-1.09, -5.2) * mm, v(-1.16, -5.25) * mm, v(-1.28, -5.25) * mm]});
            skFitSpline(sketch, "E221", {"points": [v(-1.28, -5.25) * mm, v(-1.35, -5.25) * mm, v(-1.4, -5.23) * mm, v(-1.43, -5.2) * mm]});
            skFitSpline(sketch, "E222", {"points": [v(-1.43, -5.2) * mm, v(-1.45, -5.15) * mm, v(-1.47, -5.06) * mm, v(-1.47, -4.93) * mm]});
            skFitSpline(sketch, "E223", {"points": [v(-1.47, -4.93) * mm, v(-1.47, -4.87) * mm, v(-1.46, -4.74) * mm, v(-1.45, -4.55) * mm]});
            skFitSpline(sketch, "E224", {"points": [v(-1.45, -4.55) * mm, v(-1.44, -4.36) * mm, v(-1.44, -4.2) * mm, v(-1.44, -4.08) * mm]});
            skFitSpline(sketch, "E225", {"points": [v(-1.44, -4.08) * mm, v(-1.44, -3.73) * mm, v(-1.45, -3.4) * mm, v(-1.48, -3.1) * mm]});
            skFitSpline(sketch, "E226", {"points": [v(-1.48, -3.1) * mm, v(-1.51, -2.8) * mm, v(-1.54, -2.62) * mm, v(-1.58, -2.54) * mm]});
            skFitSpline(sketch, "E227", {"points": [v(-1.58, -2.54) * mm, v(-1.6, -2.5) * mm, v(-1.62, -2.48) * mm, v(-1.64, -2.45) * mm]});
            skFitSpline(sketch, "E228", {"points": [v(-1.64, -2.45) * mm, v(-1.67, -2.42) * mm, v(-1.69, -2.4) * mm, v(-1.7, -2.38) * mm]});
            skFitSpline(sketch, "E229", {"points": [v(-1.7, -2.38) * mm, v(-1.72, -2.36) * mm, v(-1.74, -2.35) * mm, v(-1.75, -2.35) * mm]});
            skFitSpline(sketch, "E230", {"points": [v(-1.75, -2.35) * mm, v(-1.81, -2.35) * mm, v(-1.94, -2.49) * mm, v(-2.15, -2.76) * mm]});
            skFitSpline(sketch, "E231", {"points": [v(-2.15, -2.76) * mm, v(-2.35, -3.03) * mm, v(-2.51, -3.31) * mm, v(-2.65, -3.6) * mm]});
            skFitSpline(sketch, "E232", {"points": [v(-2.65, -3.6) * mm, v(-2.8, -3.9) * mm, v(-2.9, -4.12) * mm, v(-2.94, -4.25) * mm]});
            skFitSpline(sketch, "E233", {"points": [v(-2.94, -4.25) * mm, v(-2.98, -4.4) * mm, v(-3.02, -4.58) * mm, v(-3.05, -4.81) * mm]});
            skFitSpline(sketch, "E234", {"points": [v(-3.05, -4.81) * mm, v(-3.1, -5.2) * mm, v(-3.13, -5.4) * mm, v(-3.16, -5.44) * mm]});
            skFitSpline(sketch, "E235", {"points": [v(-3.16, -5.44) * mm, v(-3.18, -5.47) * mm, v(-3.2, -5.48) * mm, v(-3.23, -5.48) * mm]});
            skFitSpline(sketch, "E236", {"points": [v(-3.23, -5.48) * mm, v(-3.29, -5.47) * mm, v(-3.35, -5.43) * mm, v(-3.42, -5.35) * mm]});
            skFitSpline(sketch, "E237", {"points": [v(-3.42, -5.35) * mm, v(-3.46, -5.3) * mm, v(-3.48, -5.26) * mm, v(-3.5, -5.2) * mm]});
            skFitSpline(sketch, "E238", {"points": [v(-3.5, -5.2) * mm, v(-3.52, -5.13) * mm, v(-3.54, -5.04) * mm, v(-3.55, -4.9) * mm]});
            skFitSpline(sketch, "E239", {"points": [v(-3.55, -4.9) * mm, v(-3.56, -4.77) * mm, v(-3.57, -4.63) * mm, v(-3.58, -4.48) * mm]});
            skFitSpline(sketch, "E240", {"points": [v(-3.58, -4.48) * mm, v(-3.59, -4.32) * mm, v(-3.6, -4.1) * mm, v(-3.63, -3.81) * mm]});
            skFitSpline(sketch, "E241", {"points": [v(-3.63, -3.81) * mm, v(-3.65, -3.52) * mm, v(-3.68, -3.22) * mm, v(-3.72, -2.9) * mm]});
            skFitSpline(sketch, "E242", {"points": [v(-3.72, -2.9) * mm, v(-3.77, -2.42) * mm, v(-3.8, -2.12) * mm, v(-3.8, -2.02) * mm]});
            skLineSegment(sketch, "E243", {"start": v(-3.26, -3.01) * mm, "end": v(-3.18, -3.7) * mm});
            skLineSegment(sketch, "E244", {"start": v(-3.18, -3.7) * mm, "end": v(-3.1, -3.5) * mm});
            skFitSpline(sketch, "E245", {"points": [v(0.76, -1.87) * mm, v(0.63, -1.88) * mm, v(0.45, -1.9) * mm, v(0.23, -1.95) * mm]});
            skFitSpline(sketch, "E246", {"points": [v(0.23, -1.95) * mm, v(0, -1.98) * mm, v(-0.15, -2) * mm, v(-0.22, -2) * mm]});
            skFitSpline(sketch, "E247", {"points": [v(-0.22, -2) * mm, v(-0.4, -2) * mm, v(-0.49, -1.93) * mm, v(-0.49, -1.8) * mm]});
            skFitSpline(sketch, "E248", {"points": [v(-0.49, -1.8) * mm, v(-0.49, -1.68) * mm, v(-0.4, -1.6) * mm, v(-0.25, -1.54) * mm]});
            skFitSpline(sketch, "E249", {"points": [v(-0.25, -1.54) * mm, v(-0.1, -1.49) * mm, v(0.08, -1.44) * mm, v(0.3, -1.4) * mm]});
            skFitSpline(sketch, "E250", {"points": [v(0.3, -1.4) * mm, v(0.5, -1.38) * mm, v(0.65, -1.34) * mm, v(0.7, -1.31) * mm]});
            skFitSpline(sketch, "E251", {"points": [v(0.7, -1.31) * mm, v(0.74, -1.28) * mm, v(0.76, -1.2) * mm, v(0.76, -1.05) * mm]});
            skFitSpline(sketch, "E252", {"points": [v(0.76, -1.05) * mm, v(0.76, -0.9) * mm, v(0.74, -0.71) * mm, v(0.7, -0.48) * mm]});
            skFitSpline(sketch, "E253", {"points": [v(0.7, -0.48) * mm, v(0.67, -0.24) * mm, v(0.65, -0.03) * mm, v(0.65, 0.16) * mm]});
            skFitSpline(sketch, "E254", {"points": [v(0.65, 0.16) * mm, v(0.65, 0.3) * mm, v(0.68, 0.39) * mm, v(0.75, 0.45) * mm]});
            skFitSpline(sketch, "E255", {"points": [v(0.75, 0.45) * mm, v(0.82, 0.51) * mm, v(0.9, 0.55) * mm, v(0.98, 0.55) * mm]});
            skFitSpline(sketch, "E256", {"points": [v(0.98, 0.55) * mm, v(1.07, 0.55) * mm, v(1.13, 0.5) * mm, v(1.17, 0.44) * mm]});
            skFitSpline(sketch, "E257", {"points": [v(1.17, 0.44) * mm, v(1.19, 0.37) * mm, v(1.22, 0.1) * mm, v(1.27, -0.36) * mm]});
            skFitSpline(sketch, "E258", {"points": [v(1.27, -0.36) * mm, v(1.32, -0.83) * mm, v(1.35, -1.1) * mm, v(1.36, -1.17) * mm]});
            skFitSpline(sketch, "E259", {"points": [v(1.36, -1.17) * mm, v(1.4, -1.17) * mm, v(1.5, -1.15) * mm, v(1.68, -1.12) * mm]});
            skFitSpline(sketch, "E260", {"points": [v(1.68, -1.12) * mm, v(1.87, -1.1) * mm, v(2.01, -1.07) * mm, v(2.1, -1.07) * mm]});
            skFitSpline(sketch, "E261", {"points": [v(2.1, -1.07) * mm, v(2.25, -1.07) * mm, v(2.34, -1.1) * mm, v(2.4, -1.14) * mm]});
            skFitSpline(sketch, "E262", {"points": [v(2.4, -1.14) * mm, v(2.46, -1.19) * mm, v(2.49, -1.23) * mm, v(2.49, -1.29) * mm]});
            skFitSpline(sketch, "E263", {"points": [v(2.49, -1.29) * mm, v(2.49, -1.36) * mm, v(2.43, -1.43) * mm, v(2.33, -1.48) * mm]});
            skFitSpline(sketch, "E264", {"points": [v(2.33, -1.48) * mm, v(2.22, -1.54) * mm, v(2.03, -1.6) * mm, v(1.76, -1.67) * mm]});
            skFitSpline(sketch, "E265", {"points": [v(1.46, -2.65) * mm, v(1.49, -3.22) * mm, v(1.55, -3.75) * mm, v(1.63, -4.25) * mm]});
            skFitSpline(sketch, "E266", {"points": [v(1.63, -4.25) * mm, v(1.7, -4.75) * mm, v(1.75, -5.04) * mm, v(1.75, -5.12) * mm]});
            skFitSpline(sketch, "E267", {"points": [v(1.75, -5.12) * mm, v(1.75, -5.3) * mm, v(1.66, -5.39) * mm, v(1.47, -5.39) * mm]});
            skFitSpline(sketch, "E268", {"points": [v(1.47, -5.39) * mm, v(1.36, -5.39) * mm, v(1.28, -5.37) * mm, v(1.23, -5.33) * mm]});
            skFitSpline(sketch, "E269", {"points": [v(1.23, -5.33) * mm, v(1.1, -5.22) * mm, v(1.04, -4.99) * mm, v(1.04, -4.64) * mm]});
            skFitSpline(sketch, "E270", {"points": [v(1.04, -4.64) * mm, v(1.04, -4.5) * mm, v(1.04, -4.35) * mm, v(1.02, -4.2) * mm]});
            skFitSpline(sketch, "E271", {"points": [v(1.02, -4.2) * mm, v(1, -4.05) * mm, v(0.97, -3.82) * mm, v(0.93, -3.51) * mm]});
            skFitSpline(sketch, "E272", {"points": [v(0.93, -3.51) * mm, v(0.9, -3.2) * mm, v(0.86, -2.87) * mm, v(0.83, -2.53) * mm]});
            skFitSpline(sketch, "E273", {"points": [v(0.83, -2.53) * mm, v(0.79, -2.1) * mm, v(0.77, -1.89) * mm, v(0.76, -1.87) * mm]});
            skLineSegment(sketch, "E274", {"start": v(1.76, -1.67) * mm, "end": v(1.4, -1.72) * mm});
            skLineSegment(sketch, "E275", {"start": v(1.4, -1.72) * mm, "end": v(1.46, -2.65) * mm});
            skFitSpline(sketch, "E276", {"points": [v(3.29, -1.73) * mm, v(3.36, -1.68) * mm, v(3.42, -1.66) * mm, v(3.49, -1.66) * mm]});
            skFitSpline(sketch, "E277", {"points": [v(3.49, -1.66) * mm, v(3.55, -1.66) * mm, v(3.6, -1.69) * mm, v(3.65, -1.74) * mm]});
            skFitSpline(sketch, "E278", {"points": [v(3.65, -1.74) * mm, v(3.72, -1.86) * mm, v(3.77, -2.21) * mm, v(3.81, -2.8) * mm]});
            skFitSpline(sketch, "E279", {"points": [v(3.81, -2.8) * mm, v(3.86, -3.38) * mm, v(3.88, -3.93) * mm, v(3.88, -4.44) * mm]});
            skFitSpline(sketch, "E280", {"points": [v(3.88, -4.44) * mm, v(3.88, -4.8) * mm, v(3.87, -5) * mm, v(3.84, -5.06) * mm]});
            skFitSpline(sketch, "E281", {"points": [v(3.84, -5.06) * mm, v(3.76, -5.12) * mm, v(3.67, -5.15) * mm, v(3.58, -5.15) * mm]});
            skFitSpline(sketch, "E282", {"points": [v(3.58, -5.15) * mm, v(3.44, -5.15) * mm, v(3.35, -5.11) * mm, v(3.32, -5.03) * mm]});
            skFitSpline(sketch, "E283", {"points": [v(3.32, -5.03) * mm, v(3.3, -4.96) * mm, v(3.27, -4.54) * mm, v(3.22, -3.76) * mm]});
            skFitSpline(sketch, "E284", {"points": [v(3.22, -3.76) * mm, v(3.18, -2.98) * mm, v(3.16, -2.45) * mm, v(3.16, -2.19) * mm]});
            skFitSpline(sketch, "E285", {"points": [v(3.16, -2.19) * mm, v(3.16, -1.94) * mm, v(3.2, -1.79) * mm, v(3.29, -1.73) * mm]});
            skFitSpline(sketch, "E286", {"points": [v(3.22, -0.3) * mm, v(3.23, -0.23) * mm, v(3.26, -0.17) * mm, v(3.32, -0.12) * mm]});
            skFitSpline(sketch, "E287", {"points": [v(3.32, -0.12) * mm, v(3.38, -0.07) * mm, v(3.44, -0.05) * mm, v(3.5, -0.05) * mm]});
            skFitSpline(sketch, "E288", {"points": [v(3.5, -0.05) * mm, v(3.55, -0.05) * mm, v(3.63, -0.07) * mm, v(3.71, -0.12) * mm]});
            skFitSpline(sketch, "E289", {"points": [v(3.71, -0.12) * mm, v(3.8, -0.18) * mm, v(3.85, -0.25) * mm, v(3.85, -0.34) * mm]});
            skFitSpline(sketch, "E290", {"points": [v(3.85, -0.34) * mm, v(3.85, -0.44) * mm, v(3.82, -0.52) * mm, v(3.78, -0.6) * mm]});
            skFitSpline(sketch, "E291", {"points": [v(3.78, -0.6) * mm, v(3.73, -0.68) * mm, v(3.66, -0.72) * mm, v(3.58, -0.72) * mm]});
            skFitSpline(sketch, "E292", {"points": [v(3.58, -0.72) * mm, v(3.5, -0.72) * mm, v(3.41, -0.68) * mm, v(3.34, -0.6) * mm]});
            skFitSpline(sketch, "E293", {"points": [v(3.34, -0.6) * mm, v(3.26, -0.52) * mm, v(3.22, -0.42) * mm, v(3.22, -0.3) * mm]});
            skFitSpline(sketch, "E294", {"points": [v(4.87, -2.02) * mm, v(4.87, -1.8) * mm, v(4.94, -1.7) * mm, v(5.07, -1.7) * mm]});
            skFitSpline(sketch, "E295", {"points": [v(5.07, -1.7) * mm, v(5.16, -1.7) * mm, v(5.22, -1.76) * mm, v(5.25, -1.87) * mm]});
            skFitSpline(sketch, "E296", {"points": [v(5.25, -1.87) * mm, v(5.28, -1.97) * mm, v(5.32, -2.27) * mm, v(5.37, -2.76) * mm]});
            skFitSpline(sketch, "E297", {"points": [v(5.37, -2.76) * mm, v(5.38, -2.86) * mm, v(5.4, -2.95) * mm, v(5.4, -3.01) * mm]});
            skFitSpline(sketch, "E298", {"points": [v(5.55, -3.5) * mm, v(5.64, -3.24) * mm, v(5.71, -3.05) * mm, v(5.77, -2.93) * mm]});
            skFitSpline(sketch, "E299", {"points": [v(5.77, -2.93) * mm, v(5.84, -2.8) * mm, v(5.95, -2.63) * mm, v(6.12, -2.4) * mm]});
            skFitSpline(sketch, "E300", {"points": [v(6.12, -2.4) * mm, v(6.45, -1.97) * mm, v(6.73, -1.76) * mm, v(6.96, -1.76) * mm]});
            skFitSpline(sketch, "E301", {"points": [v(6.96, -1.76) * mm, v(7.1, -1.76) * mm, v(7.24, -1.84) * mm, v(7.35, -2) * mm]});
            skFitSpline(sketch, "E302", {"points": [v(7.35, -2) * mm, v(7.48, -2.19) * mm, v(7.56, -2.37) * mm, v(7.59, -2.55) * mm]});
            skFitSpline(sketch, "E303", {"points": [v(7.59, -2.55) * mm, v(7.62, -2.74) * mm, v(7.64, -3.16) * mm, v(7.65, -3.8) * mm]});
            skFitSpline(sketch, "E304", {"points": [v(7.65, -3.8) * mm, v(7.66, -4.22) * mm, v(7.67, -4.47) * mm, v(7.67, -4.56) * mm]});
            skFitSpline(sketch, "E305", {"points": [v(7.67, -4.56) * mm, v(7.67, -4.83) * mm, v(7.65, -5.01) * mm, v(7.61, -5.11) * mm]});
            skFitSpline(sketch, "E306", {"points": [v(7.61, -5.11) * mm, v(7.57, -5.2) * mm, v(7.5, -5.25) * mm, v(7.39, -5.25) * mm]});
            skFitSpline(sketch, "E307", {"points": [v(7.39, -5.25) * mm, v(7.3, -5.25) * mm, v(7.26, -5.23) * mm, v(7.23, -5.2) * mm]});
            skFitSpline(sketch, "E308", {"points": [v(7.23, -5.2) * mm, v(7.2, -5.15) * mm, v(7.2, -5.06) * mm, v(7.2, -4.93) * mm]});
            skFitSpline(sketch, "E309", {"points": [v(7.2, -4.93) * mm, v(7.2, -4.87) * mm, v(7.2, -4.74) * mm, v(7.2, -4.55) * mm]});
            skFitSpline(sketch, "E310", {"points": [v(7.2, -4.55) * mm, v(7.22, -4.36) * mm, v(7.22, -4.2) * mm, v(7.22, -4.08) * mm]});
            skFitSpline(sketch, "E311", {"points": [v(7.22, -4.08) * mm, v(7.22, -3.73) * mm, v(7.2, -3.4) * mm, v(7.18, -3.1) * mm]});
            skFitSpline(sketch, "E312", {"points": [v(7.18, -3.1) * mm, v(7.15, -2.8) * mm, v(7.12, -2.62) * mm, v(7.08, -2.54) * mm]});
            skFitSpline(sketch, "E313", {"points": [v(7.08, -2.54) * mm, v(7.06, -2.5) * mm, v(7.04, -2.48) * mm, v(7.02, -2.45) * mm]});
            skFitSpline(sketch, "E314", {"points": [v(7.02, -2.45) * mm, v(7, -2.42) * mm, v(6.97, -2.4) * mm, v(6.95, -2.38) * mm]});
            skFitSpline(sketch, "E315", {"points": [v(6.95, -2.38) * mm, v(6.94, -2.36) * mm, v(6.92, -2.35) * mm, v(6.92, -2.35) * mm]});
            skFitSpline(sketch, "E316", {"points": [v(6.92, -2.35) * mm, v(6.85, -2.35) * mm, v(6.72, -2.49) * mm, v(6.51, -2.76) * mm]});
            skFitSpline(sketch, "E317", {"points": [v(6.51, -2.76) * mm, v(6.32, -3.03) * mm, v(6.15, -3.31) * mm, v(6, -3.6) * mm]});
            skFitSpline(sketch, "E318", {"points": [v(6, -3.6) * mm, v(5.87, -3.9) * mm, v(5.77, -4.12) * mm, v(5.72, -4.25) * mm]});
            skFitSpline(sketch, "E319", {"points": [v(5.72, -4.25) * mm, v(5.68, -4.4) * mm, v(5.64, -4.58) * mm, v(5.61, -4.81) * mm]});
            skFitSpline(sketch, "E320", {"points": [v(5.61, -4.81) * mm, v(5.57, -5.2) * mm, v(5.53, -5.4) * mm, v(5.5, -5.44) * mm]});
            skFitSpline(sketch, "E321", {"points": [v(5.5, -5.44) * mm, v(5.48, -5.47) * mm, v(5.46, -5.48) * mm, v(5.44, -5.48) * mm]});
            skFitSpline(sketch, "E322", {"points": [v(5.44, -5.48) * mm, v(5.38, -5.47) * mm, v(5.31, -5.43) * mm, v(5.24, -5.35) * mm]});
            skFitSpline(sketch, "E323", {"points": [v(5.24, -5.35) * mm, v(5.2, -5.3) * mm, v(5.18, -5.26) * mm, v(5.16, -5.2) * mm]});
            skFitSpline(sketch, "E324", {"points": [v(5.16, -5.2) * mm, v(5.14, -5.13) * mm, v(5.13, -5.04) * mm, v(5.11, -4.9) * mm]});
            skFitSpline(sketch, "E325", {"points": [v(5.11, -4.9) * mm, v(5.1, -4.77) * mm, v(5.1, -4.63) * mm, v(5.08, -4.48) * mm]});
            skFitSpline(sketch, "E326", {"points": [v(5.08, -4.48) * mm, v(5.08, -4.32) * mm, v(5.06, -4.1) * mm, v(5.03, -3.81) * mm]});
            skFitSpline(sketch, "E327", {"points": [v(5.03, -3.81) * mm, v(5.01, -3.52) * mm, v(4.98, -3.22) * mm, v(4.94, -2.9) * mm]});
            skFitSpline(sketch, "E328", {"points": [v(4.94, -2.9) * mm, v(4.9, -2.42) * mm, v(4.87, -2.12) * mm, v(4.87, -2.02) * mm]});
            skLineSegment(sketch, "E329", {"start": v(5.4, -3.01) * mm, "end": v(5.49, -3.7) * mm});
            skLineSegment(sketch, "E330", {"start": v(5.49, -3.7) * mm, "end": v(5.55, -3.5) * mm});
            skFitSpline(sketch, "E331", {"points": [v(8.86, -3.67) * mm, v(8.86, -3.88) * mm, v(8.92, -4.08) * mm, v(9.03, -4.26) * mm]});
            skFitSpline(sketch, "E332", {"points": [v(9.03, -4.26) * mm, v(9.14, -4.44) * mm, v(9.28, -4.53) * mm, v(9.46, -4.53) * mm]});
            skFitSpline(sketch, "E333", {"points": [v(9.46, -4.53) * mm, v(9.7, -4.53) * mm, v(9.97, -4.42) * mm, v(10.26, -4.2) * mm]});
            skFitSpline(sketch, "E334", {"points": [v(10.26, -4.2) * mm, v(10.56, -3.99) * mm, v(10.8, -3.72) * mm, v(10.98, -3.39) * mm]});
            skFitSpline(sketch, "E335", {"points": [v(10.98, -3.39) * mm, v(11.08, -3.2) * mm, v(11.17, -2.98) * mm, v(11.24, -2.74) * mm]});
            skFitSpline(sketch, "E336", {"points": [v(11.24, -2.74) * mm, v(11.31, -2.5) * mm, v(11.35, -2.32) * mm, v(11.35, -2.19) * mm]});
            skFitSpline(sketch, "E337", {"points": [v(11.35, -2.19) * mm, v(11.35, -2.15) * mm, v(11.35, -2.12) * mm, v(11.34, -2.1) * mm]});
            skFitSpline(sketch, "E338", {"points": [v(11.34, -2.1) * mm, v(11.26, -2.07) * mm, v(11.12, -2.05) * mm, v(10.92, -2.05) * mm]});
            skFitSpline(sketch, "E339", {"points": [v(10.92, -2.05) * mm, v(10.73, -2.05) * mm, v(10.57, -2.07) * mm, v(10.43, -2.1) * mm]});
            skFitSpline(sketch, "E340", {"points": [v(10.43, -2.1) * mm, v(10.07, -2.2) * mm, v(9.72, -2.43) * mm, v(9.38, -2.8) * mm]});
            skFitSpline(sketch, "E341", {"points": [v(9.38, -2.8) * mm, v(9.03, -3.15) * mm, v(8.86, -3.45) * mm, v(8.86, -3.67) * mm]});
            skFitSpline(sketch, "E342", {"points": [v(11.24, -6.2) * mm, v(11.39, -6.2) * mm, v(11.46, -6.14) * mm, v(11.46, -6.01) * mm]});
            skFitSpline(sketch, "E343", {"points": [v(11.46, -6.01) * mm, v(11.46, -5.7) * mm, v(11.45, -5.44) * mm, v(11.43, -5.24) * mm]});
            skFitSpline(sketch, "E344", {"points": [v(11.43, -5.24) * mm, v(11.41, -5.04) * mm, v(11.39, -4.87) * mm, v(11.36, -4.73) * mm]});
            skFitSpline(sketch, "E345", {"points": [v(11.36, -4.73) * mm, v(11.33, -4.59) * mm, v(11.3, -4.47) * mm, v(11.3, -4.39) * mm]});
            skFitSpline(sketch, "E346", {"points": [v(11.3, -4.39) * mm, v(11.29, -4.2) * mm, v(11.27, -4.05) * mm, v(11.26, -3.94) * mm]});
            skFitSpline(sketch, "E347", {"points": [v(11.26, -3.94) * mm, v(11.14, -4.1) * mm, v(10.97, -4.26) * mm, v(10.72, -4.44) * mm]});
            skFitSpline(sketch, "E348", {"points": [v(10.72, -4.44) * mm, v(10.48, -4.62) * mm, v(10.27, -4.74) * mm, v(10.1, -4.8) * mm]});
            skFitSpline(sketch, "E349", {"points": [v(10.1, -4.8) * mm, v(9.9, -4.87) * mm, v(9.68, -4.9) * mm, v(9.45, -4.9) * mm]});
            skFitSpline(sketch, "E350", {"points": [v(9.45, -4.9) * mm, v(9.3, -4.9) * mm, v(9.18, -4.89) * mm, v(9.09, -4.86) * mm]});
            skFitSpline(sketch, "E351", {"points": [v(9.09, -4.86) * mm, v(9, -4.82) * mm, v(8.89, -4.75) * mm, v(8.75, -4.64) * mm]});
            skFitSpline(sketch, "E352", {"points": [v(8.75, -4.64) * mm, v(8.63, -4.54) * mm, v(8.54, -4.44) * mm, v(8.48, -4.35) * mm]});
            skFitSpline(sketch, "E353", {"points": [v(8.48, -4.35) * mm, v(8.43, -4.26) * mm, v(8.39, -4.14) * mm, v(8.36, -4) * mm]});
            skFitSpline(sketch, "E354", {"points": [v(8.36, -4) * mm, v(8.33, -3.84) * mm, v(8.32, -3.71) * mm, v(8.32, -3.6) * mm]});
            skFitSpline(sketch, "E355", {"points": [v(8.32, -3.6) * mm, v(8.32, -3.45) * mm, v(8.4, -3.23) * mm, v(8.54, -2.97) * mm]});
            skFitSpline(sketch, "E356", {"points": [v(8.54, -2.97) * mm, v(8.7, -2.71) * mm, v(8.82, -2.51) * mm, v(8.93, -2.38) * mm]});
            skFitSpline(sketch, "E357", {"points": [v(8.93, -2.38) * mm, v(9.02, -2.26) * mm, v(9.2, -2.13) * mm, v(9.46, -1.98) * mm]});
            skFitSpline(sketch, "E358", {"points": [v(9.46, -1.98) * mm, v(9.71, -1.83) * mm, v(9.94, -1.73) * mm, v(10.13, -1.67) * mm]});
            skFitSpline(sketch, "E359", {"points": [v(10.13, -1.67) * mm, v(10.34, -1.6) * mm, v(10.57, -1.57) * mm, v(10.84, -1.57) * mm]});
            skFitSpline(sketch, "E360", {"points": [v(10.84, -1.57) * mm, v(11.17, -1.57) * mm, v(11.44, -1.63) * mm, v(11.66, -1.74) * mm]});
            skFitSpline(sketch, "E361", {"points": [v(11.66, -1.74) * mm, v(11.88, -1.85) * mm, v(12, -2.02) * mm, v(12, -2.26) * mm]});
            skFitSpline(sketch, "E362", {"points": [v(12, -2.26) * mm, v(12, -2.39) * mm, v(11.96, -2.54) * mm, v(11.9, -2.71) * mm]});
            skFitSpline(sketch, "E363", {"points": [v(11.9, -2.71) * mm, v(11.85, -2.88) * mm, v(11.82, -3.03) * mm, v(11.82, -3.15) * mm]});
            skFitSpline(sketch, "E364", {"points": [v(11.82, -3.15) * mm, v(11.82, -3.22) * mm, v(11.82, -3.33) * mm, v(11.83, -3.47) * mm]});
            skFitSpline(sketch, "E365", {"points": [v(11.83, -3.47) * mm, v(11.84, -3.6) * mm, v(11.86, -3.83) * mm, v(11.89, -4.15) * mm]});
            skFitSpline(sketch, "E366", {"points": [v(11.89, -4.15) * mm, v(11.91, -4.47) * mm, v(11.94, -4.78) * mm, v(11.96, -5.1) * mm]});
            skFitSpline(sketch, "E367", {"points": [v(11.8, -6.56) * mm, v(11.68, -6.66) * mm, v(11.55, -6.71) * mm, v(11.41, -6.71) * mm]});
            skFitSpline(sketch, "E368", {"points": [v(11.41, -6.71) * mm, v(11.17, -6.71) * mm, v(10.87, -6.66) * mm, v(10.53, -6.55) * mm]});
            skFitSpline(sketch, "E369", {"points": [v(10.53, -6.55) * mm, v(10.2, -6.44) * mm, v(9.9, -6.3) * mm, v(9.66, -6.15) * mm]});
            skFitSpline(sketch, "E370", {"points": [v(9.66, -6.15) * mm, v(9.41, -6) * mm, v(9.3, -5.87) * mm, v(9.3, -5.76) * mm]});
            skFitSpline(sketch, "E371", {"points": [v(9.3, -5.76) * mm, v(9.3, -5.62) * mm, v(9.36, -5.46) * mm, v(9.5, -5.3) * mm]});
            skFitSpline(sketch, "E372", {"points": [v(9.5, -5.3) * mm, v(9.63, -5.14) * mm, v(9.75, -5.06) * mm, v(9.85, -5.06) * mm]});
            skFitSpline(sketch, "E373", {"points": [v(9.85, -5.06) * mm, v(10, -5.06) * mm, v(10.08, -5.11) * mm, v(10.08, -5.23) * mm]});
            skFitSpline(sketch, "E374", {"points": [v(10.08, -5.23) * mm, v(10.08, -5.28) * mm, v(10.06, -5.34) * mm, v(10.02, -5.41) * mm]});
            skFitSpline(sketch, "E375", {"points": [v(10.02, -5.41) * mm, v(9.98, -5.48) * mm, v(9.96, -5.55) * mm, v(9.96, -5.6) * mm]});
            skFitSpline(sketch, "E376", {"points": [v(9.96, -5.6) * mm, v(9.96, -5.7) * mm, v(10.03, -5.77) * mm, v(10.17, -5.84) * mm]});
            skFitSpline(sketch, "E377", {"points": [v(10.17, -5.84) * mm, v(10.3, -5.92) * mm, v(10.43, -5.95) * mm, v(10.53, -5.95) * mm]});
            skFitSpline(sketch, "E378", {"points": [v(10.53, -5.95) * mm, v(10.6, -5.95) * mm, v(10.72, -6) * mm, v(10.87, -6.07) * mm]});
            skFitSpline(sketch, "E379", {"points": [v(10.87, -6.07) * mm, v(11.02, -6.16) * mm, v(11.14, -6.2) * mm, v(11.24, -6.2) * mm]});
            skLineSegment(sketch, "E380", {"start": v(11.96, -5.1) * mm, "end": v(12.05, -6.36) * mm});
            skLineSegment(sketch, "E381", {"start": v(12.05, -6.36) * mm, "end": v(11.8, -6.56) * mm});
            skSolve(sketch);
        }
        {
            var Q0;
            Q0 = qSketchRegion(id + "F7", true);
            extrude(context, id + "F8", {"entities" : qUnion([Q0]), "operationType" : NewBodyOperationType.REMOVE, "oppositeDirection" : true, "depth" : 25 * mm});
        }
        {
            var Q0;
            Q0=qCreatedBy(makeId("Top.planeOp"),FACE);
            var sketch = newSketch(context, id + "F9", { "sketchPlane" : qUnion([Q0])});
            skLineSegment(sketch, "E382.bottom", {"start": v(0, 6.5) * mm, "end": v(6, 6.5) * mm});
            skLineSegment(sketch, "E382.top", {"start": v(0, 8.5) * mm, "end": v(6, 8.5) * mm});
            skLineSegment(sketch, "E382.left", {"start": v(0, 6.5) * mm, "end": v(0, 8.5) * mm});
            skLineSegment(sketch, "E382.right", {"start": v(6, 6.5) * mm, "end": v(6, 8.5) * mm});
            skLineSegment(sketch, "E383.bottom", {"start": v(8, -3.5) * mm, "end": v(12, -3.5) * mm});
            skLineSegment(sketch, "E383.top", {"start": v(8, -2.5) * mm, "end": v(12, -2.5) * mm});
            skLineSegment(sketch, "E383.left", {"start": v(8, -3.5) * mm, "end": v(8, -2.5) * mm});
            skLineSegment(sketch, "E383.right", {"start": v(12, -3.5) * mm, "end": v(12, -2.5) * mm});
            skLineSegment(sketch, "E384.bottom", {"start": v(-12.6, -2.5) * mm, "end": v(-9, -2.5) * mm});
            skLineSegment(sketch, "E384.top", {"start": v(-12.6, -1.5) * mm, "end": v(-9, -1.5) * mm});
            skLineSegment(sketch, "E384.left", {"start": v(-12.6, -2.5) * mm, "end": v(-12.6, -1.5) * mm});
            skLineSegment(sketch, "E384.right", {"start": v(-9, -2.5) * mm, "end": v(-9, -1.5) * mm});
            skSolve(sketch);
        }
        {
            var Q0;
            Q0=makeQuery(id+"F9.imprint","IMPRINT",FACE,{"disambiguationData":[TD([[makeQuery(id+"F9.imprint","IMPRINT",EDGE,{"derivedFrom":sQuery(id+"F9.wireOp",EDGE,"E384.bottom")}),1.0]])]});
            var Q1;
            Q1=makeQuery(id+"F9.imprint","IMPRINT",FACE,{"disambiguationData":[TD([[makeQuery(id+"F9.imprint","IMPRINT",EDGE,{"derivedFrom":sQuery(id+"F9.wireOp",EDGE,"E383.bottom")}),1.0]])]});
            var Q2;
            Q2=makeQuery(id+"F9.imprint","IMPRINT",FACE,{"disambiguationData":[TD([[makeQuery(id+"F9.imprint","IMPRINT",EDGE,{"derivedFrom":sQuery(id+"F9.wireOp",EDGE,"E382.bottom")}),1.0]])]});
            extrude(context, id + "F10", {"entities" : qUnion([Q0, Q1, Q2]), "depth" : 5 * mm});
        }
        {
            var Q0;
            Q0=makeQuery(id+"FPrQcKdI6Gvt6KK_2.9.F5.opRevolve","SWEPT_BODY",BODY,{"disambiguationData":[OSD([sQuery(id+"F4.wireOp",EDGE,"E9"),sQuery(id+"F4.wireOp",EDGE,"E10"),sQuery(id+"F4.wireOp",EDGE,"E11")])]});
            var Q1;
            Q1=makeQuery(id+"FPrQcKdI6Gvt6KK_2.8.F5.opRevolve","SWEPT_BODY",BODY,{"disambiguationData":[OSD([sQuery(id+"F4.wireOp",EDGE,"E9"),sQuery(id+"F4.wireOp",EDGE,"E10"),sQuery(id+"F4.wireOp",EDGE,"E11")])]});
            var Q2;
            Q2=makeQuery(id+"FPrQcKdI6Gvt6KK_2.7.F5.opRevolve","SWEPT_BODY",BODY,{"disambiguationData":[OSD([sQuery(id+"F4.wireOp",EDGE,"E9"),sQuery(id+"F4.wireOp",EDGE,"E10"),sQuery(id+"F4.wireOp",EDGE,"E11")])]});
            var Q3;
            Q3=makeQuery(id+"FPrQcKdI6Gvt6KK_2.6.F5.opRevolve","SWEPT_BODY",BODY,{"disambiguationData":[OSD([sQuery(id+"F4.wireOp",EDGE,"E9"),sQuery(id+"F4.wireOp",EDGE,"E10"),sQuery(id+"F4.wireOp",EDGE,"E11")])]});
            var Q4;
            Q4=makeQuery(id+"FPrQcKdI6Gvt6KK_2.5.F5.opRevolve","SWEPT_BODY",BODY,{"disambiguationData":[OSD([sQuery(id+"F4.wireOp",EDGE,"E9"),sQuery(id+"F4.wireOp",EDGE,"E10"),sQuery(id+"F4.wireOp",EDGE,"E11")])]});
            var Q5;
            Q5=makeQuery(id+"FPrQcKdI6Gvt6KK_2.4.F5.opRevolve","SWEPT_BODY",BODY,{"disambiguationData":[OSD([sQuery(id+"F4.wireOp",EDGE,"E9"),sQuery(id+"F4.wireOp",EDGE,"E10"),sQuery(id+"F4.wireOp",EDGE,"E11")])]});
            var Q6;
            Q6=makeQuery(id+"FPrQcKdI6Gvt6KK_2.3.F5.opRevolve","SWEPT_BODY",BODY,{"disambiguationData":[OSD([sQuery(id+"F4.wireOp",EDGE,"E9"),sQuery(id+"F4.wireOp",EDGE,"E10"),sQuery(id+"F4.wireOp",EDGE,"E11")])]});
            var Q7;
            Q7=makeQuery(id+"FPrQcKdI6Gvt6KK_2.2.F5.opRevolve","SWEPT_BODY",BODY,{"disambiguationData":[OSD([sQuery(id+"F4.wireOp",EDGE,"E9"),sQuery(id+"F4.wireOp",EDGE,"E10"),sQuery(id+"F4.wireOp",EDGE,"E11")])]});
            var Q8;
            Q8=makeQuery(id+"FPrQcKdI6Gvt6KK_2.1.F5.opRevolve","SWEPT_BODY",BODY,{"disambiguationData":[OSD([sQuery(id+"F4.wireOp",EDGE,"E9"),sQuery(id+"F4.wireOp",EDGE,"E10"),sQuery(id+"F4.wireOp",EDGE,"E11")])]});
            var Q9;
            Q9=makeQuery(id+"F5.opRevolve","SWEPT_BODY",BODY,{"disambiguationData":[OSD([sQuery(id+"F4.wireOp",EDGE,"E9"),sQuery(id+"F4.wireOp",EDGE,"E10"),sQuery(id+"F4.wireOp",EDGE,"E11")])]});
            var Q10;
            Q10=makeQuery(id+"FPrQcKdI6Gvt6KK_2.11.F5.opRevolve","SWEPT_BODY",BODY,{"disambiguationData":[OSD([sQuery(id+"F4.wireOp",EDGE,"E9"),sQuery(id+"F4.wireOp",EDGE,"E10"),sQuery(id+"F4.wireOp",EDGE,"E11")])]});
            var Q11;
            Q11=makeQuery(id+"FPrQcKdI6Gvt6KK_2.10.F5.opRevolve","SWEPT_BODY",BODY,{"disambiguationData":[OSD([sQuery(id+"F4.wireOp",EDGE,"E9"),sQuery(id+"F4.wireOp",EDGE,"E10"),sQuery(id+"F4.wireOp",EDGE,"E11")])]});
            var Q12;
            Q12=sQuery(id+"F0.wireOp",EDGE,"E2");
            transform(context, id + "F11", {"entities" : qUnion([Q0, Q1, Q2, Q3, Q4, Q5, Q6, Q7, Q8, Q9, Q10, Q11]), "transformType" : TransformType.ROTATION, "transformAxis" : qUnion([Q12]), "angle" : 15 * degree, "makeCopy" : false});
        }
    });
